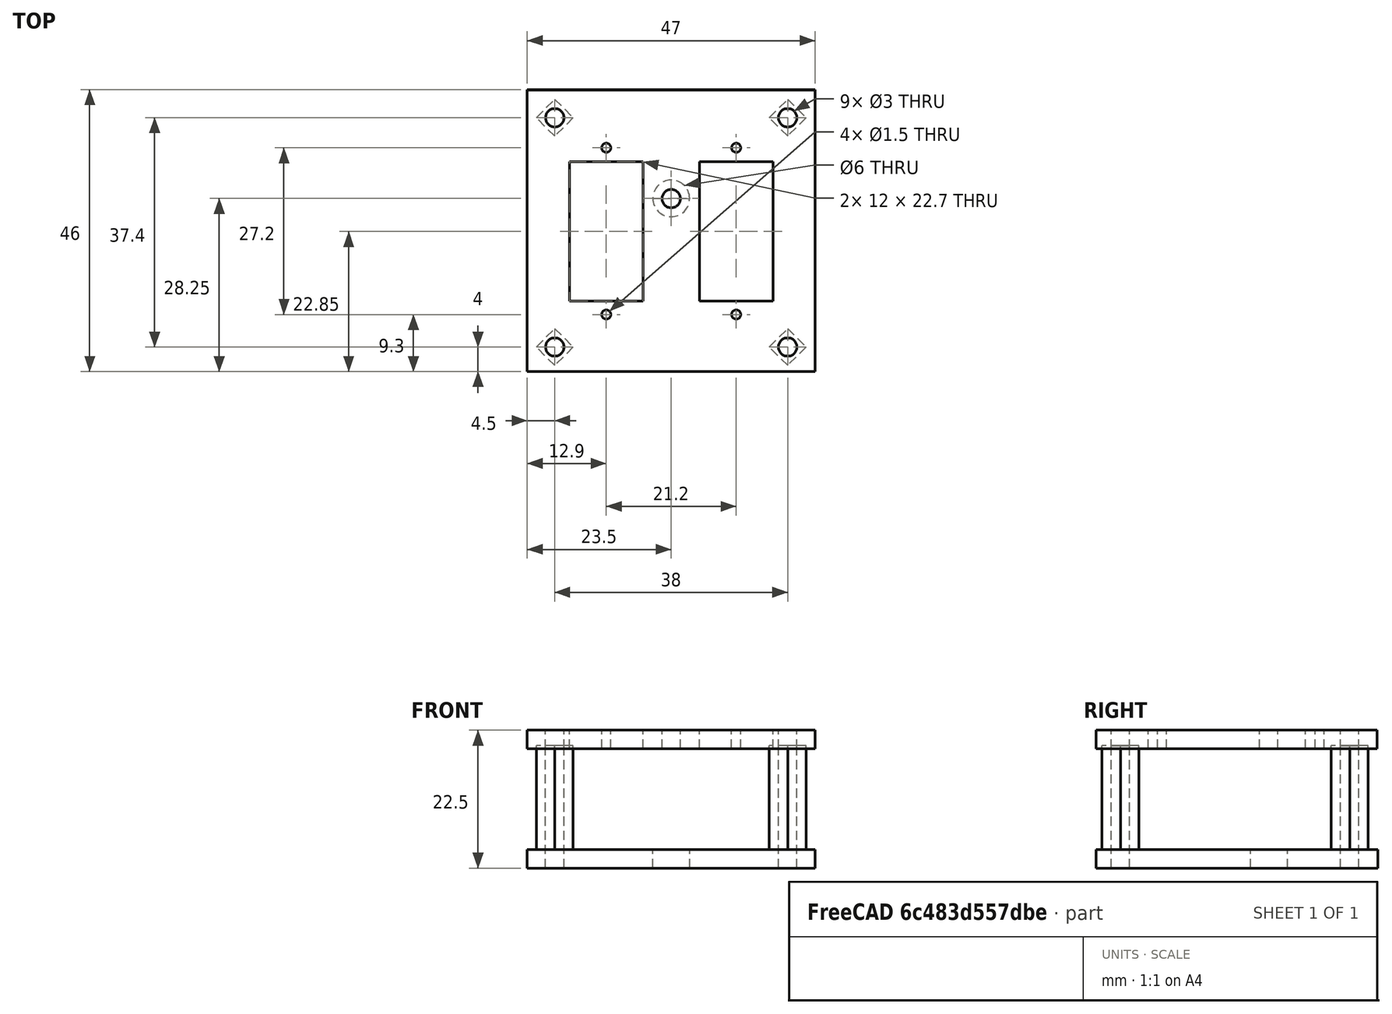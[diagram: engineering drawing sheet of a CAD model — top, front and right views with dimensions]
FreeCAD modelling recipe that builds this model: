
FCSTD DOCUMENT  (FreeCAD 0.17R13541 (Git))
Label: Base y top plate gauge
License: All rights reserved
LicenseURL: http://en.wikipedia.org/wiki/All_rights_reserved
objects: Part::Cylinder×5, Part::FeaturePython×5, Part::Box×3, Part::Fuse×2, Part::Cut×2, Part::Prism×1, Part::MultiFuse×1
note: 19 computed .brp shape members not serialized (recipe doc carries the construction recipe); baked Part::Feature solids carry a one-line shape summary decoded from their .brp

FEATURE [Part::Box] Box001  label="top plate 2"
  AttacherType = Attacher::AttachEngine3D
  Height = 3
  Length = 47
  Placement = pos=(3.25,-1.5,3) rot=(0,0,1;0rad)
  Width = 46
FEATURE [Part::Cylinder] Cylinder002  label="taladro 3"
  Angle = 360
  AttacherType = Attacher::AttachEngine3D
  Height = 10
  Placement = pos=(26.75,26.75,0) rot=(0,0,1;0rad)
  Radius = 3
FEATURE [Part::Cylinder] Cylinder003  label="taladro 4"
  Angle = 360
  AttacherType = Attacher::AttachEngine3D
  Height = 27
  Placement = pos=(7.75,2.5,0) rot=(0,0,1;0rad)
  Radius = 1.5
FEATURE [Part::FeaturePython] Array002  label="Array taladro 4"  # Draft array (typed FeaturePython)
  Angle = 360
  ArrayType = 0
  Axis = (0,0,1)
  Base = -> Cylinder003
  Center = (0,0,0)
  Fuse = false
  IntervalAxis = (0,0,0)
  IntervalX = (38,0,0)
  IntervalY = (0,37.4,0)
  IntervalZ = (0,0,0)
  NumberPolar = 1
  NumberX = 2
  NumberY = 2
  NumberZ = 1
FEATURE [Part::Prism] Prism  label="Columna"
  AttacherType = Attacher::AttachEngine3D
  Circumradius = 3
  Height = 20
  Placement = pos=(7.75,2.5,3) rot=(0,0,1;0rad)
  Polygon = 4
FEATURE [Part::FeaturePython] Array003  label="Array columnas"  # Draft array (typed FeaturePython)
  Angle = 360
  ArrayType = 0
  Axis = (0,0,1)
  Base = -> Prism
  Center = (0,0,0)
  Fuse = false
  IntervalAxis = (0,0,0)
  IntervalX = (38,0,0)
  IntervalY = (0,37.4,0)
  IntervalZ = (0,0,0)
  NumberPolar = 1
  NumberX = 2
  NumberY = 2
  NumberZ = 1
FEATURE [Part::Fuse] Fusion001  label="top plate columnas"
  Base = -> Box001
  Refine = true
  Tool = -> Array003
FEATURE [Part::Fuse] Fusion002  label="Taladros 2"
  Base = -> Cylinder002
  Refine = true
  Tool = -> Array002
FEATURE [Part::Cut] Cut001  label="Top plate final"
  Base = -> Fusion001
  Refine = true
  Tool = -> Fusion002
FEATURE [Part::Box] Box002  label="base 2"
  AttacherType = Attacher::AttachEngine3D
  Height = 3
  Length = 47
  Placement = pos=(3.25,-1.5,22.5) rot=(0,0,1;0rad)
  Width = 45.9
FEATURE [Part::Box] Box003  label="Taladro servomotor"
  AttacherType = Attacher::AttachEngine3D
  Height = 10
  Length = 12
  Placement = pos=(10.15,10,19.5) rot=(0,0,1;0rad)
  Width = 22.7
FEATURE [Part::FeaturePython] Array004  label="Array taladro servomotor"  # Draft array (typed FeaturePython)
  Angle = 360
  ArrayType = 0
  Axis = (0,0,1)
  Base = -> Box003
  Center = (0,0,0)
  Fuse = false
  IntervalAxis = (0,0,0)
  IntervalX = (21.2,0,0)
  IntervalY = (0,1,0)
  IntervalZ = (0,0,0)
  NumberPolar = 1
  NumberX = 2
  NumberY = 1
  NumberZ = 1
FEATURE [Part::Cylinder] Cylinder004  label="taladro 5"
  Angle = 360
  AttacherType = Attacher::AttachEngine3D
  Height = 10
  Placement = pos=(7.75,2.5,19.5) rot=(0,0,1;0rad)
  Radius = 1.5
FEATURE [Part::FeaturePython] Array005  label="Array taladro 5"  # Draft array (typed FeaturePython)
  Angle = 360
  ArrayType = 0
  Axis = (0,0,1)
  Base = -> Cylinder004
  Center = (0,0,0)
  Fuse = false
  IntervalAxis = (0,0,0)
  IntervalX = (38,0,0)
  IntervalY = (0,37.4,0)
  IntervalZ = (0,0,0)
  NumberPolar = 1
  NumberX = 2
  NumberY = 2
  NumberZ = 1
FEATURE [Part::Cylinder] Cylinder005  label="Taladro 6"
  Angle = 360
  AttacherType = Attacher::AttachEngine3D
  Height = 10
  Placement = pos=(26.75,26.7,19.5) rot=(0,0,1;0rad)
  Radius = 1.5
FEATURE [Part::Cylinder] Cylinder006  label="Taladro 7"
  Angle = 360
  AttacherType = Attacher::AttachEngine3D
  Height = 10
  Placement = pos=(16.15,7.8,19.5) rot=(0,0,1;0rad)
  Radius = 0.75
FEATURE [Part::FeaturePython] Array006  label="Array taladros 7"  # Draft array (typed FeaturePython)
  Angle = 360
  ArrayType = 0
  Axis = (0,0,1)
  Base = -> Cylinder006
  Center = (0,0,0)
  Fuse = false
  IntervalAxis = (0,0,0)
  IntervalX = (21.2,0,0)
  IntervalY = (0,27.2,0)
  IntervalZ = (0,0,0)
  NumberPolar = 1
  NumberX = 2
  NumberY = 2
  NumberZ = 1
FEATURE [Part::MultiFuse] Fusion003  label="Taladros 3"
  Refine = true
  Shapes = -> [Cylinder005,Array006,Array004,Array005]
FEATURE [Part::Cut] Cut002  label="base final"
  Base = -> Box002
  Refine = true
  Tool = -> Fusion003
